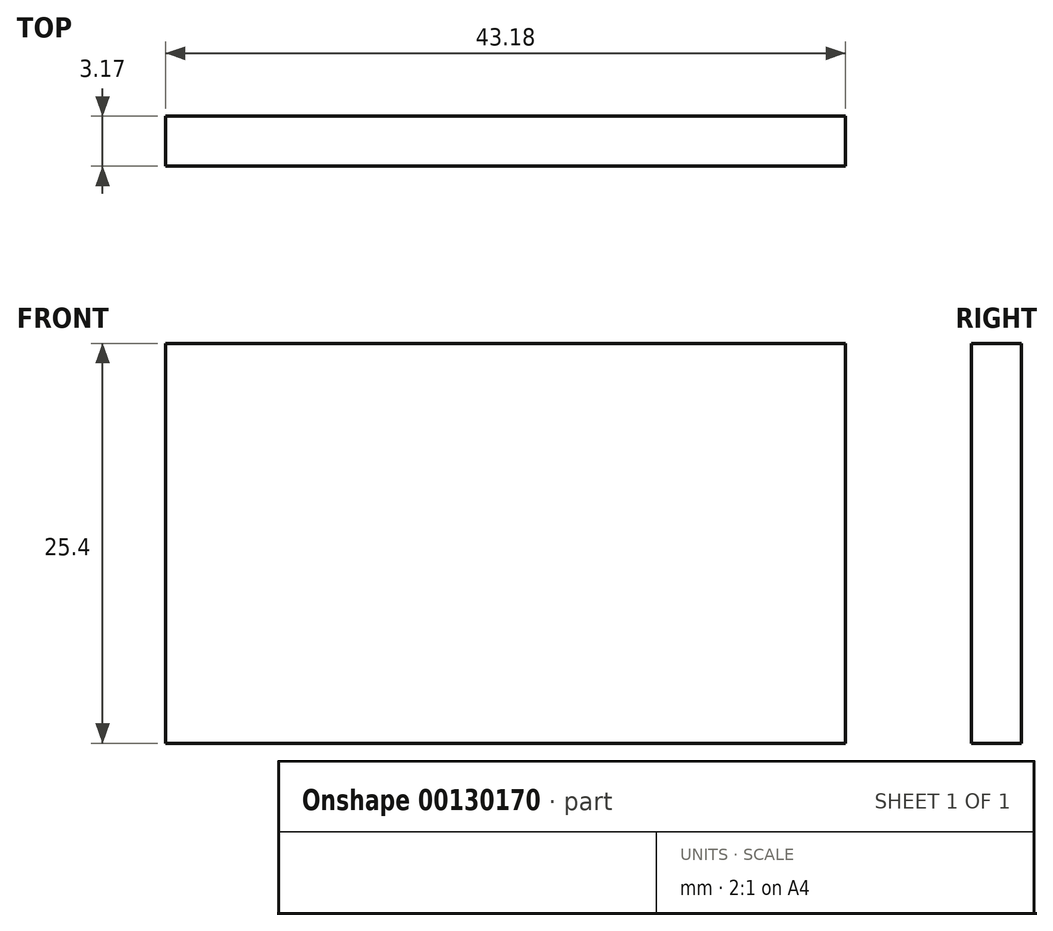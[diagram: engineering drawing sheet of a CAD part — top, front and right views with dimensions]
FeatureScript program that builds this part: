
annotation { "Feature Type Name" : "Feature", "Feature Type Description" : "" }
export const myFeature = defineFeature(function(context is Context, id is Id, definition is map)
    precondition{}
    {
        {
            var Q0;
            Q0=qCreatedBy(makeId("Front.planeOp"),FACE);
            var sketch = newSketch(context, id + "F0", { "sketchPlane" : qUnion([Q0])});
            skLineSegment(sketch, "E0.bottom", {"start": v(-32.88, 30.06) * mm, "end": v(10.3, 30.06) * mm});
            skLineSegment(sketch, "E0.top", {"start": v(-32.88, 4.66) * mm, "end": v(10.3, 4.66) * mm});
            skLineSegment(sketch, "E0.left", {"start": v(-32.88, 30.06) * mm, "end": v(-32.88, 4.66) * mm});
            skLineSegment(sketch, "E0.right", {"start": v(10.3, 30.06) * mm, "end": v(10.3, 4.66) * mm});
            skSolve(sketch);
        }
        {
            var Q0;
            Q0=makeQuery(id+"F0.imprint","IMPRINT",FACE,{"disambiguationData":[TD([[makeQuery(id+"F0.imprint","IMPRINT",EDGE,{"derivedFrom":sQuery(id+"F0.wireOp",EDGE,"E0.bottom")}),-1.0]])]});
            extrude(context, id + "F1", {"entities" : qUnion([Q0]), "depth" : 3.17 * mm});
        }
    });
